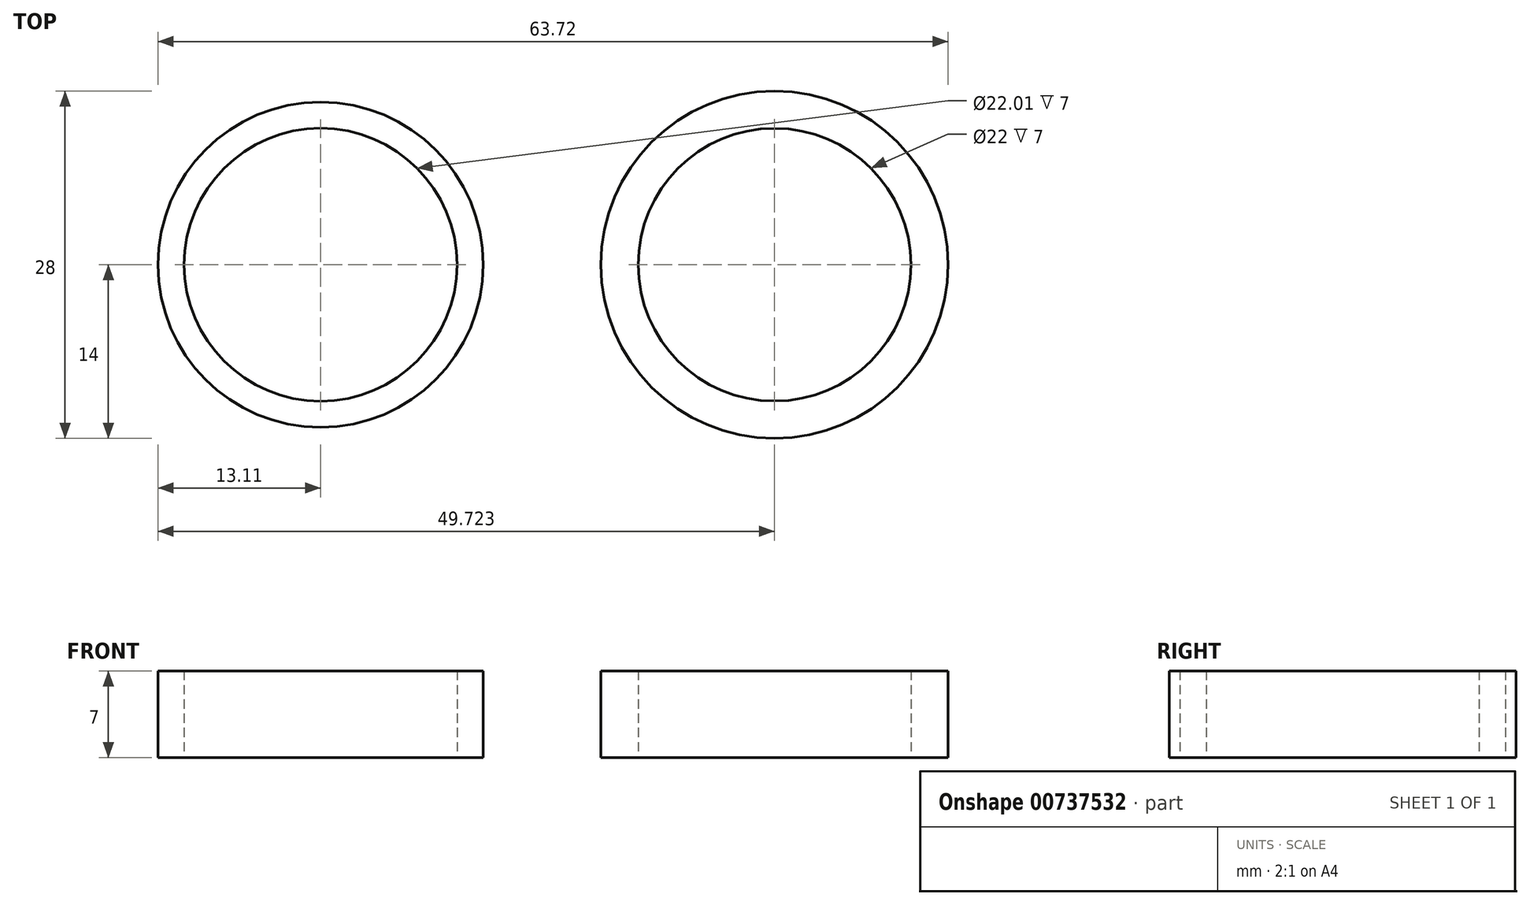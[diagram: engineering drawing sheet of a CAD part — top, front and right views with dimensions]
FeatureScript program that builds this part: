
annotation { "Feature Type Name" : "Feature", "Feature Type Description" : "" }
export const myFeature = defineFeature(function(context is Context, id is Id, definition is map)
    precondition{}
    {
        {
            var Q0;
            Q0=qCreatedBy(makeId("Top.planeOp"),FACE);
            var sketch = newSketch(context, id + "F0", { "sketchPlane" : qUnion([Q0])});
            skCircle(sketch, "E0", {"center": v(0, 0) * mm, "radius": 11 * mm});
            skCircle(sketch, "E1", {"center": v(0, 0) * mm, "radius": 13.11 * mm});
            skCircle(sketch, "E2", {"center": v(36.61, 0) * mm, "radius": 11 * mm});
            skCircle(sketch, "E3", {"center": v(36.61, 0) * mm, "radius": 14 * mm});
            skSolve(sketch);
        }
        {
            var Q0;
            Q0=makeQuery(id+"F0.imprint","IMPRINT",FACE,{"disambiguationData":[TD([[makeQuery(id+"F0.imprint","IMPRINT",EDGE,{"derivedFrom":sQuery(id+"F0.wireOp",EDGE,"E0")}),-1.0]])]});
            var Q1;
            Q1=makeQuery(id+"F0.imprint","IMPRINT",FACE,{"disambiguationData":[TD([[makeQuery(id+"F0.imprint","IMPRINT",EDGE,{"derivedFrom":sQuery(id+"F0.wireOp",EDGE,"E2")}),-1.0]])]});
            extrude(context, id + "F1", {"entities" : qUnion([Q0, Q1]), "depth" : 7 * mm, "offsetDistance" : 25 * mm});
        }
    });
